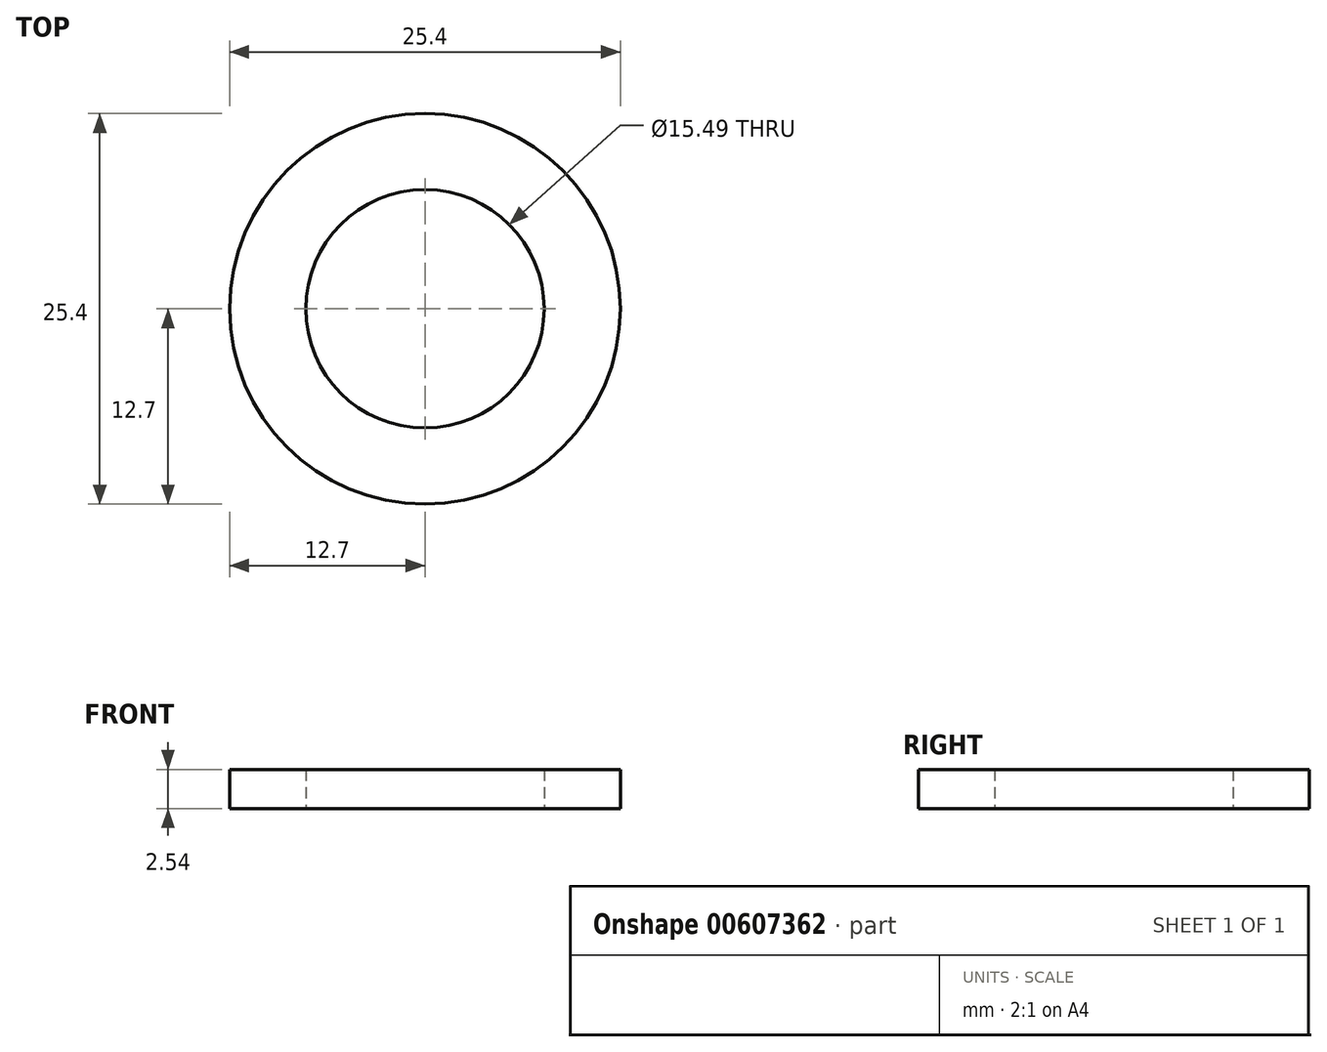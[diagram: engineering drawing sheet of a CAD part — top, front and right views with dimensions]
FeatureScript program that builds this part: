
annotation { "Feature Type Name" : "Feature", "Feature Type Description" : "" }
export const myFeature = defineFeature(function(context is Context, id is Id, definition is map)
    precondition{}
    {
        {
            var Q0;
            Q0=qCreatedBy(makeId("Top.planeOp"),FACE);
            var sketch = newSketch(context, id + "F0", { "sketchPlane" : qUnion([Q0])});
            skCircle(sketch, "E0", {"center": v(0, 0) * mm, "radius": 7.75 * mm});
            skCircle(sketch, "E1", {"center": v(0, 0) * mm, "radius": 12.7 * mm});
            skSolve(sketch);
        }
        {
            var Q0;
            Q0=makeQuery(id+"F0.imprint","IMPRINT",FACE,{"disambiguationData":[TD([[makeQuery(id+"F0.imprint","IMPRINT",EDGE,{"derivedFrom":sQuery(id+"F0.wireOp",EDGE,"E0")}),-1.0]])]});
            extrude(context, id + "F1", {"entities" : qUnion([Q0]), "depth" : 2.54 * mm, "offsetDistance" : 25.4 * mm});
        }
    });
